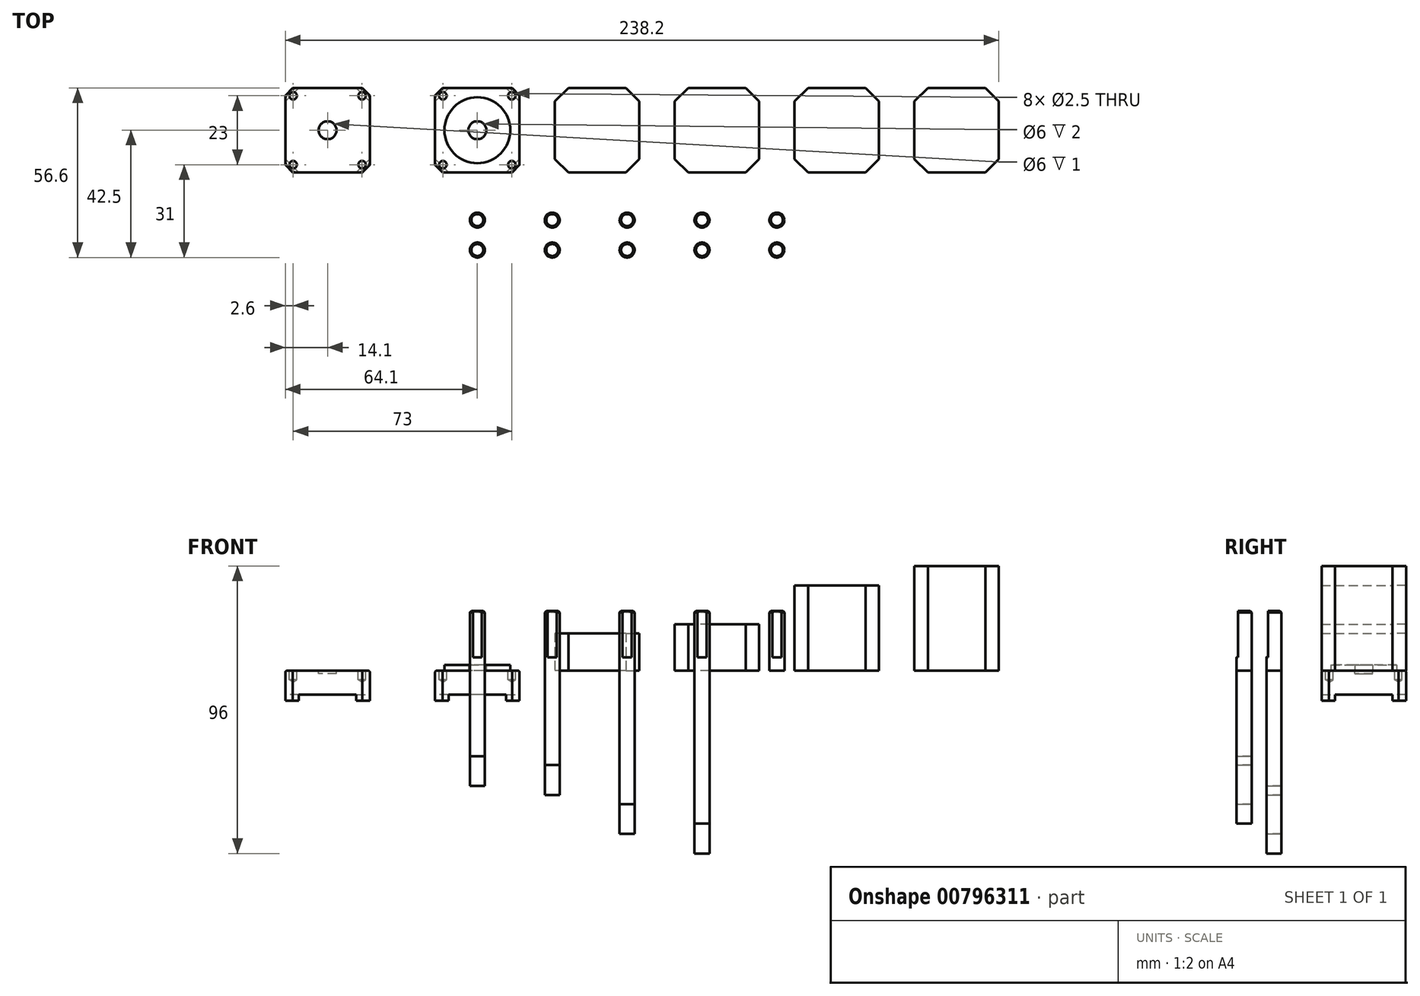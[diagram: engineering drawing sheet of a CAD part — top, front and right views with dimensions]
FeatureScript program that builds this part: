
annotation { "Feature Type Name" : "Feature", "Feature Type Description" : "" }
export const myFeature = defineFeature(function(context is Context, id is Id, definition is map)
    precondition{}
    {
        {
            var Q0;
            Q0=qCreatedBy(makeId("Top.planeOp"),FACE);
            var sketch = newSketch(context, id + "F0", { "sketchPlane" : qUnion([Q0])});
            skLineSegment(sketch, "E0.bottom", {"start": v(14.1, -14.1) * mm, "end": v(-14.1, -14.1) * mm});
            skLineSegment(sketch, "E0.top", {"start": v(14.1, 14.1) * mm, "end": v(-14.1, 14.1) * mm});
            skLineSegment(sketch, "E0.left", {"start": v(14.1, -14.1) * mm, "end": v(14.1, 14.1) * mm});
            skLineSegment(sketch, "E0.right", {"start": v(-14.1, -14.1) * mm, "end": v(-14.1, 14.1) * mm});
            skLineSegment(sketch, "E1", {"start": v(14.1, 14.1) * mm, "end": v(-14.1, -14.1) * mm, "construction": true});
            skLineSegment(sketch, "E2", {"start": v(-14.1, 14.1) * mm, "end": v(14.1, -14.1) * mm, "construction": true});
            skPoint(sketch, "E3", {"position": v(0, 0) * mm});
            skLineSegment(sketch, "E4.left", {"start": v(-11.5, 11.5) * mm, "end": v(-11.5, -11.5) * mm, "construction": true});
            skLineSegment(sketch, "E5", {"start": v(-11.5, 11.5) * mm, "end": v(11.5, 11.5) * mm, "construction": true});
            skLineSegment(sketch, "E6", {"start": v(11.5, 11.5) * mm, "end": v(11.5, -11.5) * mm, "construction": true});
            skLineSegment(sketch, "E7", {"start": v(11.5, -11.5) * mm, "end": v(-11.5, -11.5) * mm, "construction": true});
            skCircle(sketch, "E8", {"center": v(0, 0) * mm, "radius": 11 * mm});
            skCircle(sketch, "E9", {"center": v(0, 0) * mm, "radius": 3 * mm});
            skLineSegment(sketch, "E10", {"start": v(-9.6, 14.1) * mm, "end": v(-14.1, 9.6) * mm});
            skLineSegment(sketch, "E11", {"start": v(-11.6, 14.1) * mm, "end": v(-14.1, 11.6) * mm});
            skLineSegment(sketch, "E12", {"start": v(0, 0) * mm, "end": v(-11.5, 0) * mm, "construction": true});
            skLineSegment(sketch, "E13", {"start": v(0, 0) * mm, "end": v(0, 11.5) * mm, "construction": true});
            skLineSegment(sketch, "E14.MirrorCS", {"start": v(-9.6, -14.1) * mm, "end": v(-14.1, -9.6) * mm});
            skLineSegment(sketch, "E15.MirrorCS", {"start": v(-11.6, -14.1) * mm, "end": v(-14.1, -11.6) * mm});
            skLineSegment(sketch, "E16.MirrorCS", {"start": v(9.6, 14.1) * mm, "end": v(14.1, 9.6) * mm});
            skLineSegment(sketch, "E17.MirrorCS", {"start": v(11.6, 14.1) * mm, "end": v(14.1, 11.6) * mm});
            skLineSegment(sketch, "E18.MirrorCS", {"start": v(9.6, -14.1) * mm, "end": v(14.1, -9.6) * mm});
            skLineSegment(sketch, "E19.MirrorCS", {"start": v(11.6, -14.1) * mm, "end": v(14.1, -11.6) * mm});
            skPoint(sketch, "E20", {"position": v(-11.5, 11.5) * mm});
            skPoint(sketch, "E21", {"position": v(11.5, -11.5) * mm});
            skPoint(sketch, "E22", {"position": v(11.5, 11.5) * mm});
            skPoint(sketch, "E23", {"position": v(-11.5, -11.5) * mm});
            skLineSegment(sketch, "E24.1.0.0", {"start": v(-50, 0) * mm, "end": v(-50, 11.5) * mm, "construction": true});
            skCircle(sketch, "E24.1.0.1", {"center": v(-50, 0) * mm, "radius": 3 * mm});
            skLineSegment(sketch, "E24.1.0.2", {"start": v(-64.1, -14.1) * mm, "end": v(-64.1, 14.1) * mm});
            skPoint(sketch, "E24.1.0.3", {"position": v(-61.5, -11.5) * mm});
            skLineSegment(sketch, "E24.1.0.4", {"start": v(-35.9, -14.1) * mm, "end": v(-64.1, -14.1) * mm});
            skLineSegment(sketch, "E24.1.0.5", {"start": v(-61.6, -14.1) * mm, "end": v(-64.1, -11.6) * mm});
            skLineSegment(sketch, "E24.1.0.6", {"start": v(-59.6, -14.1) * mm, "end": v(-64.1, -9.6) * mm});
            skLineSegment(sketch, "E24.1.0.7", {"start": v(-40.4, -14.1) * mm, "end": v(-35.9, -9.6) * mm});
            skLineSegment(sketch, "E24.1.0.8", {"start": v(-38.4, -14.1) * mm, "end": v(-35.9, -11.6) * mm});
            skLineSegment(sketch, "E24.1.0.9", {"start": v(-35.9, -14.1) * mm, "end": v(-35.9, 14.1) * mm});
            skLineSegment(sketch, "E24.1.0.10", {"start": v(-40.4, 14.1) * mm, "end": v(-35.9, 9.6) * mm});
            skLineSegment(sketch, "E24.1.0.11", {"start": v(-38.4, 14.1) * mm, "end": v(-35.9, 11.6) * mm});
            skLineSegment(sketch, "E24.1.0.12", {"start": v(-35.9, 14.1) * mm, "end": v(-64.1, 14.1) * mm});
            skLineSegment(sketch, "E24.1.0.13", {"start": v(-59.6, 14.1) * mm, "end": v(-64.1, 9.6) * mm});
            skLineSegment(sketch, "E24.1.0.14", {"start": v(-61.6, 14.1) * mm, "end": v(-64.1, 11.6) * mm});
            skPoint(sketch, "E24.1.0.15", {"position": v(-61.5, 11.5) * mm});
            skPoint(sketch, "E24.1.0.16", {"position": v(-38.5, 11.5) * mm});
            skPoint(sketch, "E24.1.0.17", {"position": v(-38.5, -11.5) * mm});
            skLineSegment(sketch, "E24.direction1", {"start": v(0, 0) * mm, "end": v(-50, 0) * mm, "construction": true});
            skLineSegment(sketch, "E25.1.0.0", {"start": v(40, 0) * mm, "end": v(40, 11.5) * mm, "construction": true});
            skLineSegment(sketch, "E25.1.0.1", {"start": v(49.6, -14.1) * mm, "end": v(54.1, -9.6) * mm});
            skLineSegment(sketch, "E25.1.0.2", {"start": v(54.1, -14.1) * mm, "end": v(54.1, 14.1) * mm});
            skLineSegment(sketch, "E25.1.0.3", {"start": v(49.6, 14.1) * mm, "end": v(54.1, 9.6) * mm});
            skLineSegment(sketch, "E25.1.0.4", {"start": v(54.1, -14.1) * mm, "end": v(25.9, -14.1) * mm});
            skLineSegment(sketch, "E25.1.0.5", {"start": v(30.4, -14.1) * mm, "end": v(25.9, -9.6) * mm});
            skLineSegment(sketch, "E25.1.0.6", {"start": v(30.4, 14.1) * mm, "end": v(25.9, 9.6) * mm});
            skLineSegment(sketch, "E25.1.0.7", {"start": v(25.9, -14.1) * mm, "end": v(25.9, 14.1) * mm});
            skLineSegment(sketch, "E25.1.0.8", {"start": v(54.1, 14.1) * mm, "end": v(25.9, 14.1) * mm});
            skLineSegment(sketch, "E25.2.0.0", {"start": v(80, 0) * mm, "end": v(80, 11.5) * mm, "construction": true});
            skLineSegment(sketch, "E25.2.0.1", {"start": v(89.6, -14.1) * mm, "end": v(94.1, -9.6) * mm});
            skLineSegment(sketch, "E25.2.0.2", {"start": v(94.1, -14.1) * mm, "end": v(94.1, 14.1) * mm});
            skLineSegment(sketch, "E25.2.0.3", {"start": v(89.6, 14.1) * mm, "end": v(94.1, 9.6) * mm});
            skLineSegment(sketch, "E25.2.0.4", {"start": v(94.1, -14.1) * mm, "end": v(65.9, -14.1) * mm});
            skLineSegment(sketch, "E25.2.0.5", {"start": v(70.4, -14.1) * mm, "end": v(65.9, -9.6) * mm});
            skLineSegment(sketch, "E25.2.0.6", {"start": v(70.4, 14.1) * mm, "end": v(65.9, 9.6) * mm});
            skLineSegment(sketch, "E25.2.0.7", {"start": v(65.9, -14.1) * mm, "end": v(65.9, 14.1) * mm});
            skLineSegment(sketch, "E25.2.0.8", {"start": v(94.1, 14.1) * mm, "end": v(65.9, 14.1) * mm});
            skLineSegment(sketch, "E25.direction1", {"start": v(0, 0) * mm, "end": v(40, 0) * mm, "construction": true});
            skLineSegment(sketch, "E26.0.3.0", {"start": v(120, 0) * mm, "end": v(120, 11.5) * mm, "construction": true});
            skLineSegment(sketch, "E26.3.3.0", {"start": v(129.6, -14.1) * mm, "end": v(134.1, -9.6) * mm});
            skLineSegment(sketch, "E26.6.3.0", {"start": v(134.1, -14.1) * mm, "end": v(134.1, 14.1) * mm});
            skLineSegment(sketch, "E26.9.3.0", {"start": v(129.6, 14.1) * mm, "end": v(134.1, 9.6) * mm});
            skLineSegment(sketch, "E26.12.3.0", {"start": v(134.1, -14.1) * mm, "end": v(105.9, -14.1) * mm});
            skLineSegment(sketch, "E26.15.3.0", {"start": v(110.4, -14.1) * mm, "end": v(105.9, -9.6) * mm});
            skLineSegment(sketch, "E26.18.3.0", {"start": v(110.4, 14.1) * mm, "end": v(105.9, 9.6) * mm});
            skLineSegment(sketch, "E26.21.3.0", {"start": v(105.9, -14.1) * mm, "end": v(105.9, 14.1) * mm});
            skLineSegment(sketch, "E26.24.3.0", {"start": v(134.1, 14.1) * mm, "end": v(105.9, 14.1) * mm});
            skLineSegment(sketch, "E27.0.4.0", {"start": v(160, 0) * mm, "end": v(160, 11.5) * mm, "construction": true});
            skLineSegment(sketch, "E27.3.4.0", {"start": v(169.6, -14.1) * mm, "end": v(174.1, -9.6) * mm});
            skLineSegment(sketch, "E27.6.4.0", {"start": v(174.1, -14.1) * mm, "end": v(174.1, 14.1) * mm});
            skLineSegment(sketch, "E27.9.4.0", {"start": v(169.6, 14.1) * mm, "end": v(174.1, 9.6) * mm});
            skLineSegment(sketch, "E27.12.4.0", {"start": v(174.1, -14.1) * mm, "end": v(145.9, -14.1) * mm});
            skLineSegment(sketch, "E27.15.4.0", {"start": v(150.4, -14.1) * mm, "end": v(145.9, -9.6) * mm});
            skLineSegment(sketch, "E27.18.4.0", {"start": v(150.4, 14.1) * mm, "end": v(145.9, 9.6) * mm});
            skLineSegment(sketch, "E27.21.4.0", {"start": v(145.9, -14.1) * mm, "end": v(145.9, 14.1) * mm});
            skLineSegment(sketch, "E27.24.4.0", {"start": v(174.1, 14.1) * mm, "end": v(145.9, 14.1) * mm});
            skCircle(sketch, "E28", {"center": v(0, -30) * mm, "radius": 2.5 * mm});
            skCircle(sketch, "E29", {"center": v(0, -40) * mm, "radius": 2.5 * mm});
            skLineSegment(sketch, "E30", {"start": v(1.5, -42) * mm, "end": v(-1.5, -42) * mm});
            skLineSegment(sketch, "E31", {"start": v(1.5, -32) * mm, "end": v(-1.5, -32) * mm});
            skCircle(sketch, "E32.1.0.0", {"center": v(25, -40) * mm, "radius": 2.5 * mm});
            skCircle(sketch, "E32.1.0.1", {"center": v(25, -30) * mm, "radius": 2.5 * mm});
            skLineSegment(sketch, "E32.1.0.2", {"start": v(26.5, -32) * mm, "end": v(23.5, -32) * mm});
            skLineSegment(sketch, "E32.1.0.3", {"start": v(26.5, -42) * mm, "end": v(23.5, -42) * mm});
            skCircle(sketch, "E32.2.0.0", {"center": v(50, -40) * mm, "radius": 2.5 * mm});
            skCircle(sketch, "E32.2.0.1", {"center": v(50, -30) * mm, "radius": 2.5 * mm});
            skLineSegment(sketch, "E32.2.0.2", {"start": v(51.5, -32) * mm, "end": v(48.5, -32) * mm});
            skLineSegment(sketch, "E32.2.0.3", {"start": v(51.5, -42) * mm, "end": v(48.5, -42) * mm});
            skCircle(sketch, "E32.3.0.0", {"center": v(75, -40) * mm, "radius": 2.5 * mm});
            skCircle(sketch, "E32.3.0.1", {"center": v(75, -30) * mm, "radius": 2.5 * mm});
            skLineSegment(sketch, "E32.3.0.2", {"start": v(76.5, -32) * mm, "end": v(73.5, -32) * mm});
            skLineSegment(sketch, "E32.3.0.3", {"start": v(76.5, -42) * mm, "end": v(73.5, -42) * mm});
            skCircle(sketch, "E32.4.0.0", {"center": v(100, -40) * mm, "radius": 2.5 * mm});
            skCircle(sketch, "E32.4.0.1", {"center": v(100, -30) * mm, "radius": 2.5 * mm});
            skLineSegment(sketch, "E32.4.0.2", {"start": v(101.5, -32) * mm, "end": v(98.5, -32) * mm});
            skLineSegment(sketch, "E32.4.0.3", {"start": v(101.5, -42) * mm, "end": v(98.5, -42) * mm});
            skLineSegment(sketch, "E32.direction1", {"start": v(0, -40) * mm, "end": v(25, -40) * mm, "construction": true});
            skSolve(sketch);
        }
        {
            var Q0;
            Q0=makeQuery(id+"F0.imprint","IMPRINT",FACE,{"disambiguationData":[TD([[makeQuery(id+"F0.imprint","IMPRINT",EDGE,{"derivedFrom":sQuery(id+"F0.wireOp",EDGE,"E24.1.0.1")}),-1.0]])]});
            var Q1;
            Q1=makeQuery(id+"F0.imprint","IMPRINT",FACE,{"disambiguationData":[TD([[makeQuery(id+"F0.imprint","IMPRINT",EDGE,{"derivedFrom":sQuery(id+"F0.wireOp",EDGE,"E8")}),-1.0]])]});
            var Q2;
            Q2=makeQuery(id+"F0.imprint","IMPRINT",FACE,{"disambiguationData":[TD([[makeQuery(id+"F0.imprint","IMPRINT",EDGE,{"derivedFrom":sQuery(id+"F0.wireOp",EDGE,"E8")}),1.0]])]});
            var Q3;
            {var subQ0=sQuery(id+"F0.wireOp",EDGE,"E24.1.0.10");Q3=makeQuery(id+"F0.imprint","IMPRINT",FACE,{"disambiguationData":[TD([[makeQuery(id+"F0.imprint","IMPRINT",EDGE,{"derivedFrom":subQ0}),1.0]])]});}
            var Q4;
            {var subQ0=sQuery(id+"F0.wireOp",EDGE,"E24.1.0.13");Q4=makeQuery(id+"F0.imprint","IMPRINT",FACE,{"disambiguationData":[TD([[makeQuery(id+"F0.imprint","IMPRINT",EDGE,{"derivedFrom":subQ0}),-1.0]])]});}
            var Q5;
            {var subQ0=sQuery(id+"F0.wireOp",EDGE,"E24.1.0.5");Q5=makeQuery(id+"F0.imprint","IMPRINT",FACE,{"disambiguationData":[TD([[makeQuery(id+"F0.imprint","IMPRINT",EDGE,{"derivedFrom":subQ0}),-1.0]])]});}
            var Q6;
            {var subQ0=sQuery(id+"F0.wireOp",EDGE,"E24.1.0.7");Q6=makeQuery(id+"F0.imprint","IMPRINT",FACE,{"disambiguationData":[TD([[makeQuery(id+"F0.imprint","IMPRINT",EDGE,{"derivedFrom":subQ0}),-1.0]])]});}
            var Q7;
            {var subQ0=sQuery(id+"F0.wireOp",EDGE,"E14.MirrorCS");Q7=makeQuery(id+"F0.imprint","IMPRINT",FACE,{"disambiguationData":[TD([[makeQuery(id+"F0.imprint","IMPRINT",EDGE,{"derivedFrom":subQ0}),1.0]])]});}
            var Q8;
            {var subQ0=sQuery(id+"F0.wireOp",EDGE,"E10");Q8=makeQuery(id+"F0.imprint","IMPRINT",FACE,{"disambiguationData":[TD([[makeQuery(id+"F0.imprint","IMPRINT",EDGE,{"derivedFrom":subQ0}),-1.0]])]});}
            var Q9;
            {var subQ0=sQuery(id+"F0.wireOp",EDGE,"E16.MirrorCS");Q9=makeQuery(id+"F0.imprint","IMPRINT",FACE,{"disambiguationData":[TD([[makeQuery(id+"F0.imprint","IMPRINT",EDGE,{"derivedFrom":subQ0}),1.0]])]});}
            var Q10;
            {var subQ0=sQuery(id+"F0.wireOp",EDGE,"E18.MirrorCS");Q10=makeQuery(id+"F0.imprint","IMPRINT",FACE,{"disambiguationData":[TD([[makeQuery(id+"F0.imprint","IMPRINT",EDGE,{"derivedFrom":subQ0}),-1.0]])]});}
            var Q11;
            Q11=makeQuery(id+"F0.imprint","IMPRINT",FACE,{"disambiguationData":[TD([[makeQuery(id+"F0.imprint","IMPRINT",EDGE,{"derivedFrom":sQuery(id+"F0.wireOp",EDGE,"E9")}),1.0]])]});
            var Q12;
            Q12=makeQuery(id+"F0.imprint","IMPRINT",FACE,{"disambiguationData":[TD([[makeQuery(id+"F0.imprint","IMPRINT",EDGE,{"derivedFrom":sQuery(id+"F0.wireOp",EDGE,"E24.1.0.1")}),1.0]])]});
            extrude(context, id + "F1", {"entities" : qUnion([Q0, Q1, Q2, Q3, Q4, Q5, Q6, Q7, Q8, Q9, Q10, Q11, Q12]), "oppositeDirection" : true, "depth" : 8 * mm, "offsetDistance" : 25 * mm});
        }
        {
            var Q0;
            Q0=makeQuery(id+"F0.imprint","IMPRINT",FACE,{"disambiguationData":[TD([[makeQuery(id+"F0.imprint","IMPRINT",EDGE,{"derivedFrom":sQuery(id+"F0.wireOp",EDGE,"E8")}),1.0]])]});
            extrude(context, id + "F2", {"entities" : qUnion([Q0]), "operationType" : NewBodyOperationType.ADD, "depth" : 2 * mm, "offsetDistance" : 25 * mm});
        }
        {
            var Q0;
            Q0=makeQuery(id+"F0.imprint","IMPRINT",FACE,{"disambiguationData":[TD([[makeQuery(id+"F0.imprint","IMPRINT",EDGE,{"derivedFrom":sQuery(id+"F0.wireOp",EDGE,"E24.1.0.1")}),1.0]])]});
            extrude(context, id + "F3", {"entities" : qUnion([Q0]), "operationType" : NewBodyOperationType.REMOVE, "oppositeDirection" : true, "depth" : 1 * mm, "offsetDistance" : 25 * mm});
        }
        {
            var Q0;
            Q0=makeQuery(id+"F1.opExtrude","CAP_FACE",FACE,{"disambiguationData":[OSD([sQuery(id+"F0.wireOp",EDGE,"E0.bottom"),sQuery(id+"F0.wireOp",EDGE,"E0.top"),sQuery(id+"F0.wireOp",EDGE,"E0.left"),sQuery(id+"F0.wireOp",EDGE,"E0.right"),sQuery(id+"F0.wireOp",EDGE,"E11"),sQuery(id+"F0.wireOp",EDGE,"E15.MirrorCS"),sQuery(id+"F0.wireOp",EDGE,"E17.MirrorCS"),sQuery(id+"F0.wireOp",EDGE,"E19.MirrorCS")])],"isStart":false});
            var sketch = newSketch(context, id + "F4", { "sketchPlane" : qUnion([Q0])});
            skLineSegment(sketch, "E33.0", {"start": v(9.6, -14.1) * mm, "end": v(14.1, -9.6) * mm});
            skLineSegment(sketch, "E33.1", {"start": v(11.6, -14.1) * mm, "end": v(14.1, -11.6) * mm});
            skLineSegment(sketch, "E33.2", {"start": v(14.1, 11.6) * mm, "end": v(14.1, 9.6) * mm});
            skLineSegment(sketch, "E33.3", {"start": v(11.6, -14.1) * mm, "end": v(9.6, -14.1) * mm});
            skLineSegment(sketch, "E33.4", {"start": v(-9.6, -14.1) * mm, "end": v(-14.1, -9.6) * mm});
            skLineSegment(sketch, "E33.5", {"start": v(-11.6, -14.1) * mm, "end": v(-14.1, -11.6) * mm});
            skLineSegment(sketch, "E33.6", {"start": v(-14.1, 11.6) * mm, "end": v(-14.1, 9.6) * mm});
            skLineSegment(sketch, "E33.7", {"start": v(11.6, 14.1) * mm, "end": v(14.1, 11.6) * mm});
            skLineSegment(sketch, "E33.8", {"start": v(9.6, 14.1) * mm, "end": v(14.1, 9.6) * mm});
            skLineSegment(sketch, "E33.9", {"start": v(11.6, 14.1) * mm, "end": v(9.6, 14.1) * mm});
            skLineSegment(sketch, "E33.10", {"start": v(-9.6, 14.1) * mm, "end": v(-14.1, 9.6) * mm});
            skLineSegment(sketch, "E33.11", {"start": v(-11.6, 14.1) * mm, "end": v(-14.1, 11.6) * mm});
            skPoint(sketch, "E34.orphan", {"position": v(14.1, -14.1) * mm});
            skPoint(sketch, "E35.orphan", {"position": v(-14.1, -14.1) * mm});
            skLineSegment(sketch, "E36.trimOffspring", {"start": v(-14.1, -9.6) * mm, "end": v(-14.1, -11.6) * mm});
            skLineSegment(sketch, "E37.trimOffspring", {"start": v(-9.6, 14.1) * mm, "end": v(-11.6, 14.1) * mm});
            skLineSegment(sketch, "E38.trimOffspring", {"start": v(14.1, -9.6) * mm, "end": v(14.1, -11.6) * mm});
            skPoint(sketch, "E39.orphan", {"position": v(14.1, 14.1) * mm});
            skLineSegment(sketch, "E40.trimOffspring", {"start": v(-9.6, -14.1) * mm, "end": v(-11.6, -14.1) * mm});
            skPoint(sketch, "E41.orphan", {"position": v(-14.1, 14.1) * mm});
            skLineSegment(sketch, "E42.0", {"start": v(-35.9, 11.6) * mm, "end": v(-35.9, 9.6) * mm});
            skLineSegment(sketch, "E42.1", {"start": v(-40.4, -14.1) * mm, "end": v(-35.9, -9.6) * mm});
            skLineSegment(sketch, "E42.2", {"start": v(-38.4, -14.1) * mm, "end": v(-35.9, -11.6) * mm});
            skLineSegment(sketch, "E42.3", {"start": v(-38.4, -14.1) * mm, "end": v(-40.4, -14.1) * mm});
            skLineSegment(sketch, "E42.4", {"start": v(-38.4, 14.1) * mm, "end": v(-35.9, 11.6) * mm});
            skLineSegment(sketch, "E42.5", {"start": v(-40.4, 14.1) * mm, "end": v(-35.9, 9.6) * mm});
            skLineSegment(sketch, "E42.6", {"start": v(-38.4, 14.1) * mm, "end": v(-61.6, 14.1) * mm});
            skLineSegment(sketch, "E42.7", {"start": v(-59.6, -14.1) * mm, "end": v(-64.1, -9.6) * mm});
            skLineSegment(sketch, "E42.8", {"start": v(-61.6, -14.1) * mm, "end": v(-64.1, -11.6) * mm});
            skLineSegment(sketch, "E42.9", {"start": v(-64.1, 11.6) * mm, "end": v(-64.1, 9.6) * mm});
            skLineSegment(sketch, "E42.10", {"start": v(-61.6, 14.1) * mm, "end": v(-64.1, 11.6) * mm});
            skLineSegment(sketch, "E42.11", {"start": v(-59.6, 14.1) * mm, "end": v(-64.1, 9.6) * mm});
            skPoint(sketch, "E43.orphan", {"position": v(-35.9, -14.1) * mm});
            skLineSegment(sketch, "E44.trimOffspring", {"start": v(-59.6, -14.1) * mm, "end": v(-61.6, -14.1) * mm});
            skPoint(sketch, "E45.orphan", {"position": v(-64.1, -14.1) * mm});
            skLineSegment(sketch, "E46.trimOffspring", {"start": v(-64.1, -9.6) * mm, "end": v(-64.1, -11.6) * mm});
            skLineSegment(sketch, "E47.trimOffspring", {"start": v(-35.9, -9.6) * mm, "end": v(-35.9, -11.6) * mm});
            skPoint(sketch, "E48.orphan", {"position": v(-35.9, 14.1) * mm});
            skPoint(sketch, "E49.orphan", {"position": v(-64.1, 14.1) * mm});
            skSolve(sketch);
        }
        {
            var Q0;
            Q0=makeQuery(id+"F4.imprint","IMPRINT",FACE,{"disambiguationData":[TD([[makeQuery(id+"F4.imprint","IMPRINT",EDGE,{"derivedFrom":sQuery(id+"F4.wireOp",EDGE,"E42.1")}),-1.0]])]});
            var Q1;
            Q1=makeQuery(id+"F4.imprint","IMPRINT",FACE,{"disambiguationData":[TD([[makeQuery(id+"F4.imprint","IMPRINT",EDGE,{"derivedFrom":sQuery(id+"F4.wireOp",EDGE,"E42.7")}),1.0]])]});
            var Q2;
            Q2=makeQuery(id+"F4.imprint","IMPRINT",FACE,{"disambiguationData":[TD([[makeQuery(id+"F4.imprint","IMPRINT",EDGE,{"derivedFrom":sQuery(id+"F4.wireOp",EDGE,"E42.9")}),1.0]])]});
            var Q3;
            Q3=makeQuery(id+"F4.imprint","IMPRINT",FACE,{"disambiguationData":[TD([[makeQuery(id+"F4.imprint","IMPRINT",EDGE,{"derivedFrom":sQuery(id+"F4.wireOp",EDGE,"E42.0")}),-1.0]])]});
            var Q4;
            Q4=makeQuery(id+"F4.imprint","IMPRINT",FACE,{"disambiguationData":[TD([[makeQuery(id+"F4.imprint","IMPRINT",EDGE,{"derivedFrom":sQuery(id+"F4.wireOp",EDGE,"E33.4")}),1.0]])]});
            var Q5;
            Q5=makeQuery(id+"F4.imprint","IMPRINT",FACE,{"disambiguationData":[TD([[makeQuery(id+"F4.imprint","IMPRINT",EDGE,{"derivedFrom":sQuery(id+"F4.wireOp",EDGE,"E33.0")}),-1.0]])]});
            var Q6;
            Q6=makeQuery(id+"F4.imprint","IMPRINT",FACE,{"disambiguationData":[TD([[makeQuery(id+"F4.imprint","IMPRINT",EDGE,{"derivedFrom":sQuery(id+"F4.wireOp",EDGE,"E33.2")}),-1.0]])]});
            var Q7;
            Q7=makeQuery(id+"F4.imprint","IMPRINT",FACE,{"disambiguationData":[TD([[makeQuery(id+"F4.imprint","IMPRINT",EDGE,{"derivedFrom":sQuery(id+"F4.wireOp",EDGE,"E33.6")}),1.0]])]});
            extrude(context, id + "F5", {"entities" : qUnion([Q0, Q1, Q2, Q3, Q4, Q5, Q6, Q7]), "operationType" : NewBodyOperationType.ADD, "depth" : 2 * mm, "offsetDistance" : 25 * mm});
        }
        {
            var Q0;
            Q0=sQuery(id+"F0.wireOp",VERTEX,"E23");
            var Q1;
            Q1=sQuery(id+"F0.wireOp",VERTEX,"E21");
            var Q2;
            Q2=sQuery(id+"F0.wireOp",VERTEX,"E22");
            var Q3;
            Q3=sQuery(id+"F0.wireOp",VERTEX,"E20");
            var Q4;
            Q4=sQuery(id+"F0.wireOp",VERTEX,"E24.1.0.17");
            var Q5;
            Q5=sQuery(id+"F0.wireOp",VERTEX,"E24.1.0.16");
            var Q6;
            Q6=sQuery(id+"F0.wireOp",VERTEX,"E24.1.0.15");
            var Q7;
            Q7=sQuery(id+"F0.wireOp",VERTEX,"E24.1.0.3");
            var Q8;
            Q8=makeQuery(id+"F1.opExtrude","SWEPT_BODY",BODY,{"disambiguationData":[OSD([sQuery(id+"F0.wireOp",EDGE,"E0.bottom"),sQuery(id+"F0.wireOp",EDGE,"E0.top"),sQuery(id+"F0.wireOp",EDGE,"E0.left"),sQuery(id+"F0.wireOp",EDGE,"E0.right"),sQuery(id+"F0.wireOp",EDGE,"E11"),sQuery(id+"F0.wireOp",EDGE,"E15.MirrorCS"),sQuery(id+"F0.wireOp",EDGE,"E17.MirrorCS"),sQuery(id+"F0.wireOp",EDGE,"E19.MirrorCS")])]});
            var Q9;
            Q9=makeQuery(id+"F1.opExtrude","SWEPT_BODY",BODY,{"disambiguationData":[OSD([sQuery(id+"F0.wireOp",EDGE,"E24.1.0.2"),sQuery(id+"F0.wireOp",EDGE,"E24.1.0.4"),sQuery(id+"F0.wireOp",EDGE,"E24.1.0.5"),sQuery(id+"F0.wireOp",EDGE,"E24.1.0.8"),sQuery(id+"F0.wireOp",EDGE,"E24.1.0.9"),sQuery(id+"F0.wireOp",EDGE,"E24.1.0.11"),sQuery(id+"F0.wireOp",EDGE,"E24.1.0.12"),sQuery(id+"F0.wireOp",EDGE,"E24.1.0.14")])]});
            hole(context, id + "F6", {"style" : HoleStyle.SIMPLE, "endStyle" : HoleEndStyle.BLIND, "holeDiameter" : 2.5 * mm, "majorDiameter" : 5 * mm, "holeDepth" : 3 * mm, "isTappedThrough" : true, "tappedDepth" : 3.5 * mm, "tapClearance" : 3, "locations" : qUnion([Q0, Q1, Q2, Q3, Q4, Q5, Q6, Q7]), "scope" : qUnion([Q8, Q9])});
        }
        {
            var Q0;
            {var subQ1=sQuery(id+"F0.wireOp",EDGE,"E25.1.0.1");Q0=makeQuery(id+"F0.imprint","IMPRINT",FACE,{"disambiguationData":[TD([[makeQuery(id+"F0.imprint","IMPRINT",EDGE,{"derivedFrom":subQ1}),1.0]])]});}
            extrude(context, id + "F7", {"entities" : qUnion([Q0]), "depth" : (28.5 - 2 * 8) * mm, "offsetDistance" : 25 * mm});
        }
        {
            var Q0;
            {var subQ1=sQuery(id+"F0.wireOp",EDGE,"E25.2.0.1");Q0=makeQuery(id+"F0.imprint","IMPRINT",FACE,{"disambiguationData":[TD([[makeQuery(id+"F0.imprint","IMPRINT",EDGE,{"derivedFrom":subQ1}),1.0]])]});}
            extrude(context, id + "F8", {"entities" : qUnion([Q0]), "depth" : (31.5 - 2 * 8) * mm, "offsetDistance" : 25 * mm});
        }
        {
            var Q0;
            {var subQ1=sQuery(id+"F0.wireOp",EDGE,"E26.3.3.0");Q0=makeQuery(id+"F0.imprint","IMPRINT",FACE,{"disambiguationData":[TD([[makeQuery(id+"F0.imprint","IMPRINT",EDGE,{"derivedFrom":subQ1}),1.0]])]});}
            extrude(context, id + "F9", {"entities" : qUnion([Q0]), "depth" : (44.5 - 2 * 8) * mm, "offsetDistance" : 25 * mm});
        }
        {
            var Q0;
            {var subQ1=sQuery(id+"F0.wireOp",EDGE,"E27.3.4.0");Q0=makeQuery(id+"F0.imprint","IMPRINT",FACE,{"disambiguationData":[TD([[makeQuery(id+"F0.imprint","IMPRINT",EDGE,{"derivedFrom":subQ1}),1.0]])]});}
            extrude(context, id + "F10", {"entities" : qUnion([Q0]), "depth" : (51 - 2 * 8) * mm, "offsetDistance" : 25 * mm});
        }
        {
            var Q0;
            {var subQ0=sQuery(id+"F0.wireOp",EDGE,"E30");Q0=makeQuery(id+"F0.imprint","IMPRINT",FACE,{"disambiguationData":[TD([[makeQuery(id+"F0.imprint","IMPRINT",EDGE,{"derivedFrom":subQ0}),1.0]])]});}
            var Q1;
            {var subQ0=sQuery(id+"F0.wireOp",EDGE,"E30");Q1=makeQuery(id+"F0.imprint","IMPRINT",FACE,{"disambiguationData":[TD([[makeQuery(id+"F0.imprint","IMPRINT",EDGE,{"derivedFrom":subQ0}),-1.0]])]});}
            var Q2;
            Q2=makeQuery(id+"F0.imprint","IMPRINT",FACE,{"disambiguationData":[TD([[makeQuery(id+"F0.imprint","IMPRINT",EDGE,{"derivedFrom":sQuery(id+"F0.wireOp",EDGE,"E28")}),1.0]])]});
            var Q3;
            Q3=makeQuery(id+"F0.imprint","IMPRINT",FACE,{"disambiguationData":[TD([[makeQuery(id+"F0.imprint","IMPRINT",EDGE,{"derivedFrom":sQuery(id+"F0.wireOp",EDGE,"2f0729d9-fa48-4009-a288-3bd3fb485b2e.1.0.1")}),1.0]])]});
            var Q4;
            {var subQ0=sQuery(id+"F0.wireOp",EDGE,"2f0729d9-fa48-4009-a288-3bd3fb485b2e.1.0.2");Q4=makeQuery(id+"F0.imprint","IMPRINT",FACE,{"disambiguationData":[TD([[makeQuery(id+"F0.imprint","IMPRINT",EDGE,{"derivedFrom":subQ0}),-1.0]])]});}
            var Q5;
            {var subQ0=sQuery(id+"F0.wireOp",EDGE,"2f0729d9-fa48-4009-a288-3bd3fb485b2e.1.0.2");Q5=makeQuery(id+"F0.imprint","IMPRINT",FACE,{"disambiguationData":[TD([[makeQuery(id+"F0.imprint","IMPRINT",EDGE,{"derivedFrom":subQ0}),1.0]])]});}
            var Q6;
            {var subQ0=sQuery(id+"F0.wireOp",EDGE,"2f0729d9-fa48-4009-a288-3bd3fb485b2e.2.0.2");Q6=makeQuery(id+"F0.imprint","IMPRINT",FACE,{"disambiguationData":[TD([[makeQuery(id+"F0.imprint","IMPRINT",EDGE,{"derivedFrom":subQ0}),-1.0]])]});}
            var Q7;
            Q7=makeQuery(id+"F0.imprint","IMPRINT",FACE,{"disambiguationData":[TD([[makeQuery(id+"F0.imprint","IMPRINT",EDGE,{"derivedFrom":sQuery(id+"F0.wireOp",EDGE,"2f0729d9-fa48-4009-a288-3bd3fb485b2e.2.0.1")}),1.0]])]});
            var Q8;
            {var subQ0=sQuery(id+"F0.wireOp",EDGE,"2f0729d9-fa48-4009-a288-3bd3fb485b2e.2.0.2");Q8=makeQuery(id+"F0.imprint","IMPRINT",FACE,{"disambiguationData":[TD([[makeQuery(id+"F0.imprint","IMPRINT",EDGE,{"derivedFrom":subQ0}),1.0]])]});}
            var Q9;
            {var subQ0=sQuery(id+"F0.wireOp",EDGE,"2f0729d9-fa48-4009-a288-3bd3fb485b2e.3.0.2");Q9=makeQuery(id+"F0.imprint","IMPRINT",FACE,{"disambiguationData":[TD([[makeQuery(id+"F0.imprint","IMPRINT",EDGE,{"derivedFrom":subQ0}),-1.0]])]});}
            var Q10;
            Q10=makeQuery(id+"F0.imprint","IMPRINT",FACE,{"disambiguationData":[TD([[makeQuery(id+"F0.imprint","IMPRINT",EDGE,{"derivedFrom":sQuery(id+"F0.wireOp",EDGE,"2f0729d9-fa48-4009-a288-3bd3fb485b2e.3.0.1")}),1.0]])]});
            var Q11;
            {var subQ0=sQuery(id+"F0.wireOp",EDGE,"2f0729d9-fa48-4009-a288-3bd3fb485b2e.3.0.2");Q11=makeQuery(id+"F0.imprint","IMPRINT",FACE,{"disambiguationData":[TD([[makeQuery(id+"F0.imprint","IMPRINT",EDGE,{"derivedFrom":subQ0}),1.0]])]});}
            var Q12;
            {var subQ0=sQuery(id+"F0.wireOp",EDGE,"2f0729d9-fa48-4009-a288-3bd3fb485b2e.4.0.2");Q12=makeQuery(id+"F0.imprint","IMPRINT",FACE,{"disambiguationData":[TD([[makeQuery(id+"F0.imprint","IMPRINT",EDGE,{"derivedFrom":subQ0}),-1.0]])]});}
            var Q13;
            Q13=makeQuery(id+"F0.imprint","IMPRINT",FACE,{"disambiguationData":[TD([[makeQuery(id+"F0.imprint","IMPRINT",EDGE,{"derivedFrom":sQuery(id+"F0.wireOp",EDGE,"2f0729d9-fa48-4009-a288-3bd3fb485b2e.4.0.1")}),1.0]])]});
            var Q14;
            {var subQ0=sQuery(id+"F0.wireOp",EDGE,"2f0729d9-fa48-4009-a288-3bd3fb485b2e.4.0.2");Q14=makeQuery(id+"F0.imprint","IMPRINT",FACE,{"disambiguationData":[TD([[makeQuery(id+"F0.imprint","IMPRINT",EDGE,{"derivedFrom":subQ0}),1.0]])]});}
            var Q15;
            {var subQ0=sQuery(id+"F0.wireOp",EDGE,"E32.1.0.3");Q15=makeQuery(id+"F0.imprint","IMPRINT",FACE,{"disambiguationData":[TD([[makeQuery(id+"F0.imprint","IMPRINT",EDGE,{"derivedFrom":subQ0}),-1.0]])]});}
            var Q16;
            {var subQ0=sQuery(id+"F0.wireOp",EDGE,"E32.1.0.3");Q16=makeQuery(id+"F0.imprint","IMPRINT",FACE,{"disambiguationData":[TD([[makeQuery(id+"F0.imprint","IMPRINT",EDGE,{"derivedFrom":subQ0}),1.0]])]});}
            var Q17;
            {var subQ0=sQuery(id+"F0.wireOp",EDGE,"E32.1.0.2");Q17=makeQuery(id+"F0.imprint","IMPRINT",FACE,{"disambiguationData":[TD([[makeQuery(id+"F0.imprint","IMPRINT",EDGE,{"derivedFrom":subQ0}),-1.0]])]});}
            var Q18;
            {var subQ0=sQuery(id+"F0.wireOp",EDGE,"E32.1.0.2");Q18=makeQuery(id+"F0.imprint","IMPRINT",FACE,{"disambiguationData":[TD([[makeQuery(id+"F0.imprint","IMPRINT",EDGE,{"derivedFrom":subQ0}),1.0]])]});}
            var Q19;
            {var subQ0=sQuery(id+"F0.wireOp",EDGE,"E32.2.0.2");Q19=makeQuery(id+"F0.imprint","IMPRINT",FACE,{"disambiguationData":[TD([[makeQuery(id+"F0.imprint","IMPRINT",EDGE,{"derivedFrom":subQ0}),-1.0]])]});}
            var Q20;
            {var subQ0=sQuery(id+"F0.wireOp",EDGE,"E32.2.0.2");Q20=makeQuery(id+"F0.imprint","IMPRINT",FACE,{"disambiguationData":[TD([[makeQuery(id+"F0.imprint","IMPRINT",EDGE,{"derivedFrom":subQ0}),1.0]])]});}
            var Q21;
            {var subQ0=sQuery(id+"F0.wireOp",EDGE,"E32.2.0.3");Q21=makeQuery(id+"F0.imprint","IMPRINT",FACE,{"disambiguationData":[TD([[makeQuery(id+"F0.imprint","IMPRINT",EDGE,{"derivedFrom":subQ0}),-1.0]])]});}
            var Q22;
            {var subQ0=sQuery(id+"F0.wireOp",EDGE,"E32.2.0.3");Q22=makeQuery(id+"F0.imprint","IMPRINT",FACE,{"disambiguationData":[TD([[makeQuery(id+"F0.imprint","IMPRINT",EDGE,{"derivedFrom":subQ0}),1.0]])]});}
            var Q23;
            {var subQ0=sQuery(id+"F0.wireOp",EDGE,"E32.4.0.2");Q23=makeQuery(id+"F0.imprint","IMPRINT",FACE,{"disambiguationData":[TD([[makeQuery(id+"F0.imprint","IMPRINT",EDGE,{"derivedFrom":subQ0}),1.0]])]});}
            var Q24;
            {var subQ0=sQuery(id+"F0.wireOp",EDGE,"E32.4.0.2");Q24=makeQuery(id+"F0.imprint","IMPRINT",FACE,{"disambiguationData":[TD([[makeQuery(id+"F0.imprint","IMPRINT",EDGE,{"derivedFrom":subQ0}),-1.0]])]});}
            var Q25;
            {var subQ0=sQuery(id+"F0.wireOp",EDGE,"E32.4.0.3");Q25=makeQuery(id+"F0.imprint","IMPRINT",FACE,{"disambiguationData":[TD([[makeQuery(id+"F0.imprint","IMPRINT",EDGE,{"derivedFrom":subQ0}),-1.0]])]});}
            var Q26;
            {var subQ0=sQuery(id+"F0.wireOp",EDGE,"E32.4.0.3");Q26=makeQuery(id+"F0.imprint","IMPRINT",FACE,{"disambiguationData":[TD([[makeQuery(id+"F0.imprint","IMPRINT",EDGE,{"derivedFrom":subQ0}),1.0]])]});}
            var Q27;
            {var subQ0=sQuery(id+"F0.wireOp",EDGE,"E32.3.0.2");Q27=makeQuery(id+"F0.imprint","IMPRINT",FACE,{"disambiguationData":[TD([[makeQuery(id+"F0.imprint","IMPRINT",EDGE,{"derivedFrom":subQ0}),-1.0]])]});}
            var Q28;
            {var subQ0=sQuery(id+"F0.wireOp",EDGE,"E32.3.0.2");Q28=makeQuery(id+"F0.imprint","IMPRINT",FACE,{"disambiguationData":[TD([[makeQuery(id+"F0.imprint","IMPRINT",EDGE,{"derivedFrom":subQ0}),1.0]])]});}
            var Q29;
            {var subQ0=sQuery(id+"F0.wireOp",EDGE,"E32.3.0.3");Q29=makeQuery(id+"F0.imprint","IMPRINT",FACE,{"disambiguationData":[TD([[makeQuery(id+"F0.imprint","IMPRINT",EDGE,{"derivedFrom":subQ0}),-1.0]])]});}
            var Q30;
            {var subQ0=sQuery(id+"F0.wireOp",EDGE,"E32.3.0.3");Q30=makeQuery(id+"F0.imprint","IMPRINT",FACE,{"disambiguationData":[TD([[makeQuery(id+"F0.imprint","IMPRINT",EDGE,{"derivedFrom":subQ0}),1.0]])]});}
            extrude(context, id + "F11", {"entities" : qUnion([Q0, Q1, Q2, Q3, Q4, Q5, Q6, Q7, Q8, Q9, Q10, Q11, Q12, Q13, Q14, Q15, Q16, Q17, Q18, Q19, Q20, Q21, Q22, Q23, Q24, Q25, Q26, Q27, Q28, Q29, Q30]), "depth" : 20 * mm, "offsetDistance" : 25 * mm});
        }
        {
            var Q0;
            Q0=makeQuery(id+"F11.opExtrude","CAP_FACE",FACE,{"disambiguationData":[OSD([sQuery(id+"F0.wireOp",EDGE,"E32.4.0.0")])],"isStart":false});
            var sketch = newSketch(context, id + "F12", { "sketchPlane" : qUnion([Q0])});
            skLineSegment(sketch, "E50.0", {"start": v(101.5, -42) * mm, "end": v(98.5, -42) * mm});
            skLineSegment(sketch, "E51.0", {"start": v(76.5, -42) * mm, "end": v(73.5, -42) * mm});
            skLineSegment(sketch, "E52.0", {"start": v(101.5, -32) * mm, "end": v(98.5, -32) * mm});
            skLineSegment(sketch, "E53.0", {"start": v(76.5, -32) * mm, "end": v(73.5, -32) * mm});
            skLineSegment(sketch, "E54.0", {"start": v(51.5, -32) * mm, "end": v(48.5, -32) * mm});
            skLineSegment(sketch, "E55.0", {"start": v(51.5, -42) * mm, "end": v(48.5, -42) * mm});
            skLineSegment(sketch, "E56.0", {"start": v(26.5, -42) * mm, "end": v(23.5, -42) * mm});
            skLineSegment(sketch, "E57.0", {"start": v(26.5, -32) * mm, "end": v(23.5, -32) * mm});
            skLineSegment(sketch, "E58.0", {"start": v(1.5, -32) * mm, "end": v(-1.5, -32) * mm});
            skLineSegment(sketch, "E59.0", {"start": v(1.5, -42) * mm, "end": v(-1.5, -42) * mm});
            skArc(sketch, "E60.0", {"start": v(-1.5, -32) * mm, "mid": v(0, -32.5) * mm, "end": v(1.5, -32) * mm});
            skArc(sketch, "E61.0", {"start": v(-1.5, -42) * mm, "mid": v(0, -42.5) * mm, "end": v(1.5, -42) * mm});
            skArc(sketch, "E62.0", {"start": v(23.5, -32) * mm, "mid": v(25, -32.5) * mm, "end": v(26.5, -32) * mm});
            skArc(sketch, "E63.0", {"start": v(23.5, -42) * mm, "mid": v(25, -42.5) * mm, "end": v(26.5, -42) * mm});
            skArc(sketch, "E64.0", {"start": v(48.5, -32) * mm, "mid": v(50, -32.5) * mm, "end": v(51.5, -32) * mm});
            skArc(sketch, "E65.0", {"start": v(48.5, -42) * mm, "mid": v(50, -42.5) * mm, "end": v(51.5, -42) * mm});
            skArc(sketch, "E66.0", {"start": v(73.5, -32) * mm, "mid": v(75, -32.5) * mm, "end": v(76.5, -32) * mm});
            skArc(sketch, "E67.0", {"start": v(73.5, -42) * mm, "mid": v(75, -42.5) * mm, "end": v(76.5, -42) * mm});
            skArc(sketch, "E68.0", {"start": v(98.5, -32) * mm, "mid": v(100, -32.5) * mm, "end": v(101.5, -32) * mm});
            skArc(sketch, "E69.0", {"start": v(98.5, -42) * mm, "mid": v(100, -42.5) * mm, "end": v(101.5, -42) * mm});
            skSolve(sketch);
        }
        {
            var Q0;
            Q0=makeQuery(id+"F12.imprint","IMPRINT",FACE,{"disambiguationData":[TD([[makeQuery(id+"F12.imprint","IMPRINT",EDGE,{"derivedFrom":sQuery(id+"F12.wireOp",EDGE,"E52.0")}),1.0]])]});
            var Q1;
            Q1=makeQuery(id+"F12.imprint","IMPRINT",FACE,{"disambiguationData":[TD([[makeQuery(id+"F12.imprint","IMPRINT",EDGE,{"derivedFrom":sQuery(id+"F12.wireOp",EDGE,"E50.0")}),1.0]])]});
            var Q2;
            Q2=makeQuery(id+"F12.imprint","IMPRINT",FACE,{"disambiguationData":[TD([[makeQuery(id+"F12.imprint","IMPRINT",EDGE,{"derivedFrom":sQuery(id+"F12.wireOp",EDGE,"E51.0")}),1.0]])]});
            var Q3;
            Q3=makeQuery(id+"F12.imprint","IMPRINT",FACE,{"disambiguationData":[TD([[makeQuery(id+"F12.imprint","IMPRINT",EDGE,{"derivedFrom":sQuery(id+"F12.wireOp",EDGE,"E53.0")}),1.0]])]});
            var Q4;
            Q4=makeQuery(id+"F12.imprint","IMPRINT",FACE,{"disambiguationData":[TD([[makeQuery(id+"F12.imprint","IMPRINT",EDGE,{"derivedFrom":sQuery(id+"F12.wireOp",EDGE,"E54.0")}),1.0]])]});
            var Q5;
            Q5=makeQuery(id+"F12.imprint","IMPRINT",FACE,{"disambiguationData":[TD([[makeQuery(id+"F12.imprint","IMPRINT",EDGE,{"derivedFrom":sQuery(id+"F12.wireOp",EDGE,"E55.0")}),1.0]])]});
            var Q6;
            Q6=makeQuery(id+"F12.imprint","IMPRINT",FACE,{"disambiguationData":[TD([[makeQuery(id+"F12.imprint","IMPRINT",EDGE,{"derivedFrom":sQuery(id+"F12.wireOp",EDGE,"E57.0")}),1.0]])]});
            var Q7;
            Q7=makeQuery(id+"F12.imprint","IMPRINT",FACE,{"disambiguationData":[TD([[makeQuery(id+"F12.imprint","IMPRINT",EDGE,{"derivedFrom":sQuery(id+"F12.wireOp",EDGE,"E56.0")}),1.0]])]});
            var Q8;
            Q8=makeQuery(id+"F12.imprint","IMPRINT",FACE,{"disambiguationData":[TD([[makeQuery(id+"F12.imprint","IMPRINT",EDGE,{"derivedFrom":sQuery(id+"F12.wireOp",EDGE,"E58.0")}),1.0]])]});
            var Q9;
            Q9=makeQuery(id+"F12.imprint","IMPRINT",FACE,{"disambiguationData":[TD([[makeQuery(id+"F12.imprint","IMPRINT",EDGE,{"derivedFrom":sQuery(id+"F12.wireOp",EDGE,"E59.0")}),1.0]])]});
            extrude(context, id + "F13", {"entities" : qUnion([Q0, Q1, Q2, Q3, Q4, Q5, Q6, Q7, Q8, Q9]), "operationType" : NewBodyOperationType.REMOVE, "oppositeDirection" : true, "depth" : 15.5 * mm, "offsetDistance" : 25 * mm});
        }
        {
            var Q0;
            Q0=makeQuery(id+"F1.opExtrude","CAP_EDGE",EDGE,{"disambiguationData":[OSD([sQuery(id+"F0.wireOp",EDGE,"E24.1.0.9")])],"isStart":true});
            var Q1;
            Q1=makeQuery(id+"F1.opExtrude","CAP_EDGE",EDGE,{"disambiguationData":[OSD([sQuery(id+"F0.wireOp",EDGE,"E24.1.0.8")])],"isStart":true});
            var Q2;
            Q2=makeQuery(id+"F1.opExtrude","CAP_EDGE",EDGE,{"disambiguationData":[OSD([sQuery(id+"F0.wireOp",EDGE,"E24.1.0.5")])],"isStart":true});
            var Q3;
            Q3=makeQuery(id+"F1.opExtrude","CAP_EDGE",EDGE,{"disambiguationData":[OSD([sQuery(id+"F0.wireOp",EDGE,"E24.1.0.2")])],"isStart":true});
            var Q4;
            Q4=makeQuery(id+"F1.opExtrude","CAP_EDGE",EDGE,{"disambiguationData":[OSD([sQuery(id+"F0.wireOp",EDGE,"E24.1.0.4")])],"isStart":true});
            var Q5;
            Q5=makeQuery(id+"F1.opExtrude","CAP_EDGE",EDGE,{"disambiguationData":[OSD([sQuery(id+"F0.wireOp",EDGE,"E24.1.0.12")])],"isStart":true});
            var Q6;
            Q6=makeQuery(id+"F1.opExtrude","CAP_EDGE",EDGE,{"disambiguationData":[OSD([sQuery(id+"F0.wireOp",EDGE,"E24.1.0.11")])],"isStart":true});
            var Q7;
            Q7=makeQuery(id+"F1.opExtrude","CAP_EDGE",EDGE,{"disambiguationData":[OSD([sQuery(id+"F0.wireOp",EDGE,"E24.1.0.14")])],"isStart":true});
            var Q8;
            Q8=makeQuery(id+"F1.opExtrude","CAP_EDGE",EDGE,{"disambiguationData":[OSD([sQuery(id+"F0.wireOp",EDGE,"E0.right")])],"isStart":true});
            var Q9;
            Q9=makeQuery(id+"F1.opExtrude","CAP_EDGE",EDGE,{"disambiguationData":[OSD([sQuery(id+"F0.wireOp",EDGE,"E15.MirrorCS")])],"isStart":true});
            var Q10;
            Q10=makeQuery(id+"F1.opExtrude","CAP_EDGE",EDGE,{"disambiguationData":[OSD([sQuery(id+"F0.wireOp",EDGE,"E0.bottom")])],"isStart":true});
            var Q11;
            Q11=makeQuery(id+"F1.opExtrude","CAP_EDGE",EDGE,{"disambiguationData":[OSD([sQuery(id+"F0.wireOp",EDGE,"E19.MirrorCS")])],"isStart":true});
            var Q12;
            Q12=makeQuery(id+"F1.opExtrude","CAP_EDGE",EDGE,{"disambiguationData":[OSD([sQuery(id+"F0.wireOp",EDGE,"E0.left")])],"isStart":true});
            var Q13;
            Q13=makeQuery(id+"F1.opExtrude","CAP_EDGE",EDGE,{"disambiguationData":[OSD([sQuery(id+"F0.wireOp",EDGE,"E17.MirrorCS")])],"isStart":true});
            var Q14;
            Q14=makeQuery(id+"F1.opExtrude","CAP_EDGE",EDGE,{"disambiguationData":[OSD([sQuery(id+"F0.wireOp",EDGE,"E0.top")])],"isStart":true});
            var Q15;
            Q15=makeQuery(id+"F1.opExtrude","CAP_EDGE",EDGE,{"disambiguationData":[OSD([sQuery(id+"F0.wireOp",EDGE,"E11")])],"isStart":true});
            fillet(context, id + "F14", {"entities" : qUnion([Q0, Q1, Q2, Q3, Q4, Q5, Q6, Q7, Q8, Q9, Q10, Q11, Q12, Q13, Q14, Q15]), "radius" : 0.5 * mm, "tangentPropagation" : true, "allowEdgeOverflow" : false});
        }
        {
            var Q0;
            Q0=makeQuery(id+"F11.opExtrude","CAP_EDGE",EDGE,{"disambiguationData":[OSD([sQuery(id+"F0.wireOp",EDGE,"E29")])],"isStart":false});
            var Q1;
            Q1=makeQuery(id+"F11.opExtrude","CAP_EDGE",EDGE,{"disambiguationData":[OSD([sQuery(id+"F0.wireOp",EDGE,"E28")])],"isStart":false});
            var Q2;
            Q2=makeQuery(id+"F11.opExtrude","CAP_EDGE",EDGE,{"disambiguationData":[OSD([sQuery(id+"F0.wireOp",EDGE,"E32.1.0.1")])],"isStart":false});
            var Q3;
            Q3=makeQuery(id+"F11.opExtrude","CAP_EDGE",EDGE,{"disambiguationData":[OSD([sQuery(id+"F0.wireOp",EDGE,"E32.1.0.0")])],"isStart":false});
            var Q4;
            Q4=makeQuery(id+"F11.opExtrude","CAP_EDGE",EDGE,{"disambiguationData":[OSD([sQuery(id+"F0.wireOp",EDGE,"E32.2.0.0")])],"isStart":false});
            var Q5;
            Q5=makeQuery(id+"F11.opExtrude","CAP_EDGE",EDGE,{"disambiguationData":[OSD([sQuery(id+"F0.wireOp",EDGE,"E32.2.0.1")])],"isStart":false});
            var Q6;
            Q6=makeQuery(id+"F11.opExtrude","CAP_EDGE",EDGE,{"disambiguationData":[OSD([sQuery(id+"F0.wireOp",EDGE,"E32.3.0.1")])],"isStart":false});
            var Q7;
            Q7=makeQuery(id+"F11.opExtrude","CAP_EDGE",EDGE,{"disambiguationData":[OSD([sQuery(id+"F0.wireOp",EDGE,"E32.3.0.0")])],"isStart":false});
            var Q8;
            Q8=makeQuery(id+"F11.opExtrude","CAP_EDGE",EDGE,{"disambiguationData":[OSD([sQuery(id+"F0.wireOp",EDGE,"E32.4.0.0")])],"isStart":false});
            var Q9;
            Q9=makeQuery(id+"F11.opExtrude","CAP_EDGE",EDGE,{"disambiguationData":[OSD([sQuery(id+"F0.wireOp",EDGE,"E32.4.0.1")])],"isStart":false});
            chamfer(context, id + "F15", {"entities" : qUnion([Q0, Q1, Q2, Q3, Q4, Q5, Q6, Q7, Q8, Q9]), "width" : 0.5 * mm});
        }
        {
            var Q0;
            Q0=makeQuery(id+"F11.opExtrude","CAP_FACE",FACE,{"disambiguationData":[OSD([sQuery(id+"F0.wireOp",EDGE,"E29")])],"isStart":true});
            extrude(context, id + "F16", {"entities" : qUnion([Q0]), "operationType" : NewBodyOperationType.ADD, "depth" : 28.5 * mm, "offsetDistance" : 25 * mm});
        }
        {
            var Q0;
            Q0=makeQuery(id+"F11.opExtrude","CAP_FACE",FACE,{"disambiguationData":[OSD([sQuery(id+"F0.wireOp",EDGE,"E28")])],"isStart":true});
            extrude(context, id + "F17", {"entities" : qUnion([Q0]), "operationType" : NewBodyOperationType.ADD, "depth" : (28.5 + 10) * mm, "offsetDistance" : 25 * mm});
        }
        {
            var Q0;
            Q0=makeQuery(id+"F11.opExtrude","CAP_FACE",FACE,{"disambiguationData":[OSD([sQuery(id+"F0.wireOp",EDGE,"E32.1.0.0")])],"isStart":true});
            extrude(context, id + "F18", {"entities" : qUnion([Q0]), "operationType" : NewBodyOperationType.ADD, "depth" : 31.5 * mm, "offsetDistance" : 25 * mm});
        }
        {
            var Q0;
            Q0=makeQuery(id+"F11.opExtrude","CAP_FACE",FACE,{"disambiguationData":[OSD([sQuery(id+"F0.wireOp",EDGE,"E32.1.0.1")])],"isStart":true});
            extrude(context, id + "F19", {"entities" : qUnion([Q0]), "operationType" : NewBodyOperationType.ADD, "depth" : 41.5 * mm, "offsetDistance" : 25 * mm});
        }
        {
            var Q0;
            Q0=makeQuery(id+"F11.opExtrude","CAP_FACE",FACE,{"disambiguationData":[OSD([sQuery(id+"F0.wireOp",EDGE,"E32.2.0.0")])],"isStart":true});
            extrude(context, id + "F20", {"entities" : qUnion([Q0]), "operationType" : NewBodyOperationType.ADD, "depth" : 44.5 * mm, "offsetDistance" : 25 * mm});
        }
        {
            var Q0;
            Q0=makeQuery(id+"F11.opExtrude","CAP_FACE",FACE,{"disambiguationData":[OSD([sQuery(id+"F0.wireOp",EDGE,"E32.2.0.1")])],"isStart":true});
            extrude(context, id + "F21", {"entities" : qUnion([Q0]), "operationType" : NewBodyOperationType.ADD, "depth" : 54.5 * mm, "offsetDistance" : 25 * mm});
        }
        {
            var Q0;
            Q0=makeQuery(id+"F11.opExtrude","CAP_FACE",FACE,{"disambiguationData":[OSD([sQuery(id+"F0.wireOp",EDGE,"E32.3.0.0")])],"isStart":true});
            extrude(context, id + "F22", {"entities" : qUnion([Q0]), "operationType" : NewBodyOperationType.ADD, "depth" : 51 * mm, "offsetDistance" : 25 * mm});
        }
        {
            var Q0;
            Q0=makeQuery(id+"F11.opExtrude","CAP_FACE",FACE,{"disambiguationData":[OSD([sQuery(id+"F0.wireOp",EDGE,"E32.3.0.1")])],"isStart":true});
            extrude(context, id + "F23", {"entities" : qUnion([Q0]), "operationType" : NewBodyOperationType.ADD, "depth" : 61 * mm, "offsetDistance" : 25 * mm});
        }
    });
